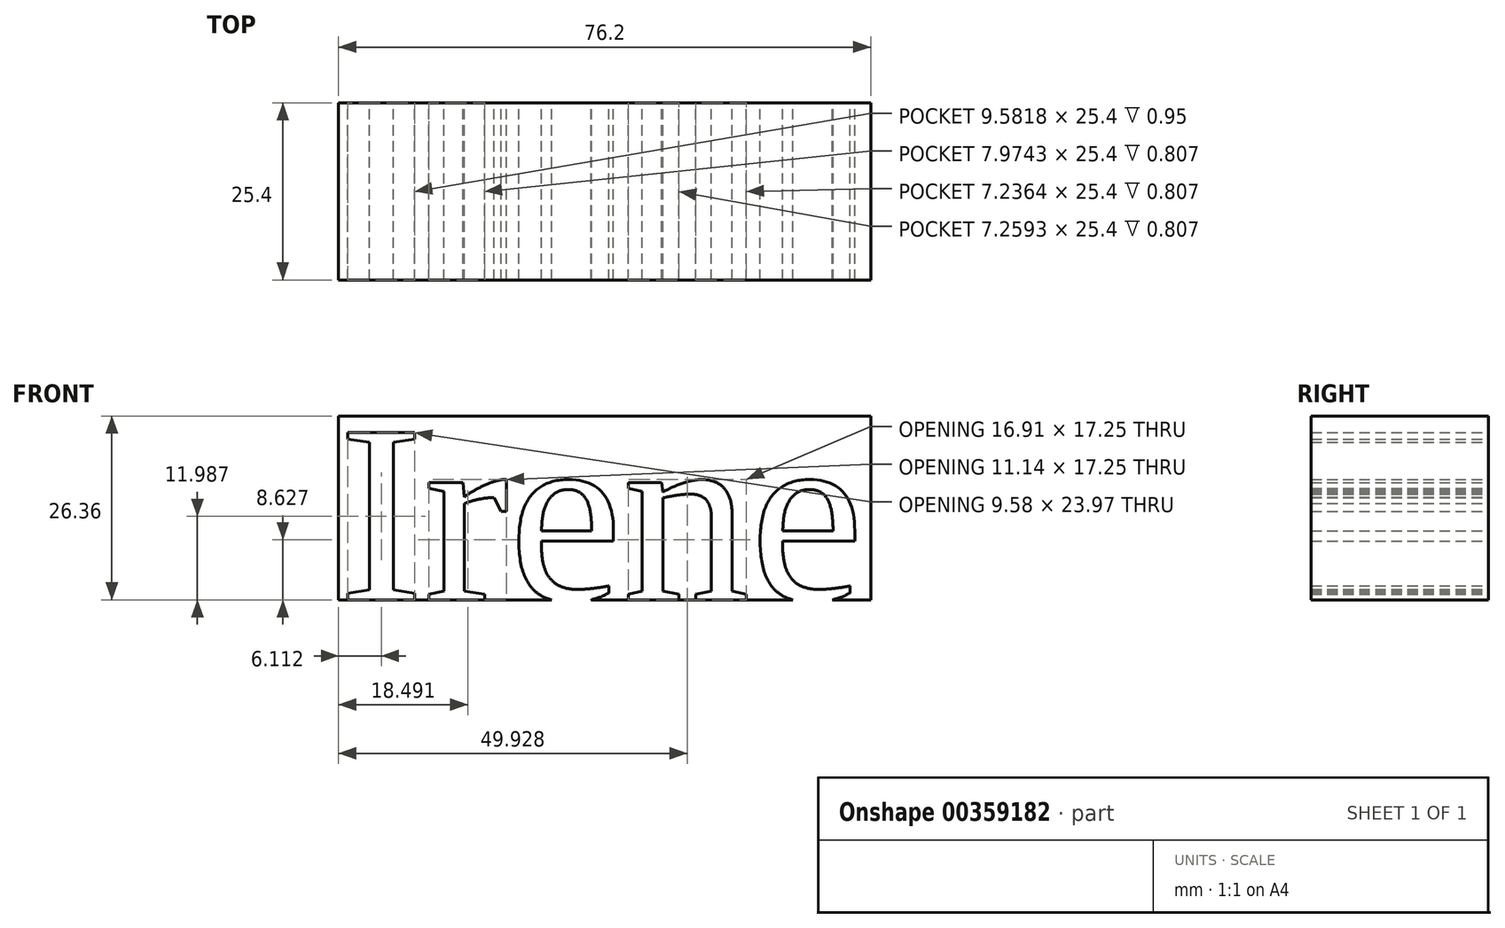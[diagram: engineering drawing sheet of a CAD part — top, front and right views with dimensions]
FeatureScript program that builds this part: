
annotation { "Feature Type Name" : "Feature", "Feature Type Description" : "" }
export const myFeature = defineFeature(function(context is Context, id is Id, definition is map)
    precondition{}
    {
        {
            var Q0;
            Q0=qCreatedBy(makeId("Front.planeOp"),FACE);
            var sketch = newSketch(context, id + "F0", { "sketchPlane" : qUnion([Q0])});
            skText(sketch, "E0", { "text": "Irene", "fontName": "Tinos-Regular.ttf"});
            skLineSegment(sketch, "E1.bottom", {"start": v(-38.8, 27.1) * mm, "end": v(37.4, 27.1) * mm});
            skLineSegment(sketch, "E1.top", {"start": v(-38.8, 0.75) * mm, "end": v(37.4, 0.75) * mm});
            skLineSegment(sketch, "E1.left", {"start": v(-38.8, 27.1) * mm, "end": v(-38.8, 0.75) * mm});
            skLineSegment(sketch, "E1.right", {"start": v(37.4, 27.1) * mm, "end": v(37.4, 0.75) * mm});
            const initialGuessF0  = {"E0": [-0.0388, 0.00075, 1, 0, 0.02636]};
            skSetInitialGuess(sketch, initialGuessF0);
            skSolve(sketch);
        }
        {
            var Q0;
            Q0=makeQuery(id+"F0.imprint","IMPRINT",FACE,{"disambiguationData":[TD([[makeQuery(id+"F0.imprint","IMPRINT",EDGE,{"derivedFrom":sQuery(id+"F0.wireOp",EDGE,"E0.sketch_text.stroke-0")}),1.0]])]});
            var Q1;
            {var subQ0=sQuery(id+"F0.wireOp",EDGE,"E0.sketch_text.stroke-60");Q1=makeQuery(id+"F0.imprint","IMPRINT",FACE,{"disambiguationData":[TD([[makeQuery(id+"F0.imprint","IMPRINT",EDGE,{"derivedFrom":subQ0}),1.0]])]});}
            var Q2;
            Q2=makeQuery(id+"F0.imprint","IMPRINT",FACE,{"disambiguationData":[TD([[makeQuery(id+"F0.imprint","IMPRINT",EDGE,{"derivedFrom":sQuery(id+"F0.wireOp",EDGE,"E0.sketch_text.stroke-93")}),1.0]])]});
            var Q3;
            Q3=makeQuery(id+"F0.imprint","IMPRINT",FACE,{"disambiguationData":[TD([[makeQuery(id+"F0.imprint","IMPRINT",EDGE,{"derivedFrom":sQuery(id+"F0.wireOp",EDGE,"E0.sketch_text.stroke-47")}),1.0]])]});
            extrude(context, id + "F1", {"entities" : qUnion([Q0, Q1, Q2, Q3]), "depth" : 25.4 * mm});
        }
    });
